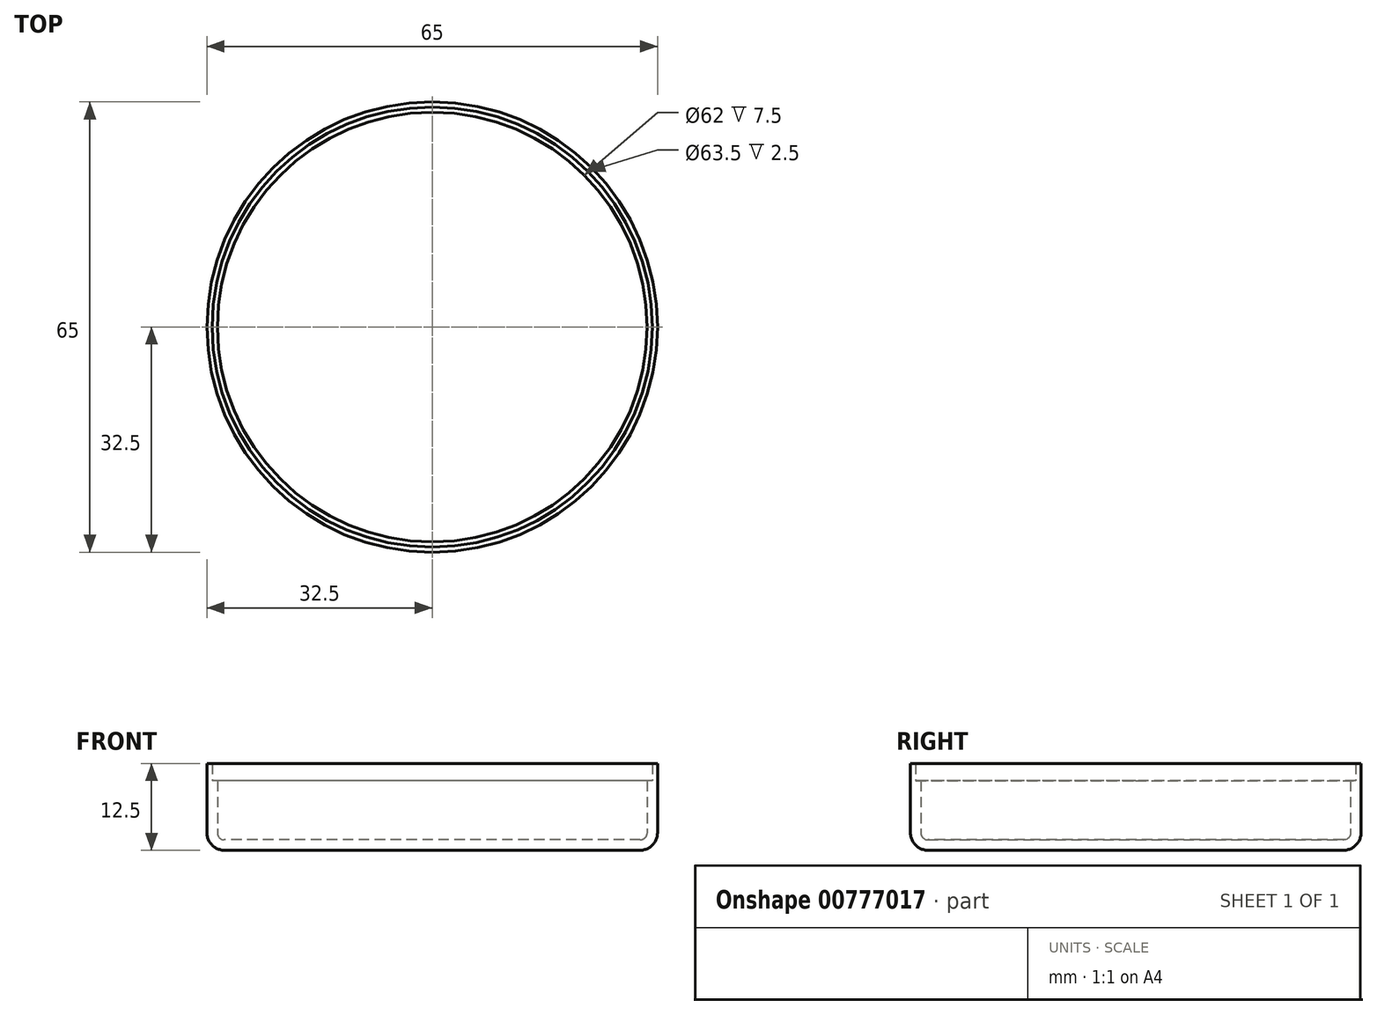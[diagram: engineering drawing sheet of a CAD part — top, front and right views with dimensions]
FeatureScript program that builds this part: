
annotation { "Feature Type Name" : "Feature", "Feature Type Description" : "" }
export const myFeature = defineFeature(function(context is Context, id is Id, definition is map)
    precondition{}
    {
        {
            var Q0;
            Q0=qCreatedBy(makeId("Top.planeOp"),FACE);
            var sketch = newSketch(context, id + "F0", { "sketchPlane" : qUnion([Q0])});
            skCircle(sketch, "E0", {"center": v(0, 0) * mm, "radius": 32.5 * mm});
            skSolve(sketch);
        }
        {
            var Q0;
            Q0=qSketchRegion(id+"F0",true);
            extrude(context, id + "F1", {"entities" : qUnion([Q0]), "depth" : 10 * mm, "offsetDistance" : 25 * mm});
        }
        {
            var Q0;
            Q0=makeQuery(id+"F1.opExtrude","CAP_FACE",FACE,{"disambiguationData":[OSD([sQuery(id+"F0.wireOp",EDGE,"pcHNsLAs-uuIG-92PN-J4nV-sG1yAEwh4vms.bottom"),sQuery(id+"F0.wireOp",EDGE,"pcHNsLAs-uuIG-92PN-J4nV-sG1yAEwh4vms.top"),sQuery(id+"F0.wireOp",EDGE,"pcHNsLAs-uuIG-92PN-J4nV-sG1yAEwh4vms.left"),sQuery(id+"F0.wireOp",EDGE,"pcHNsLAs-uuIG-92PN-J4nV-sG1yAEwh4vms.right"),sQuery(id+"F0.wireOp",EDGE,"3d6bdb04-9177-4708-87b0-630207d0257c.filletArc"),sQuery(id+"F0.wireOp",EDGE,"a6119fb4-ba20-4dce-af5d-a38932c804a4.filletArc"),sQuery(id+"F0.wireOp",EDGE,"7038d429-74eb-4160-9e18-919da026d677.filletArc"),sQuery(id+"F0.wireOp",EDGE,"e058b54d-4a7d-470c-b5c4-87012d02d3e7.filletArc")])],"isStart":true});
            var Q1;
            Q1=makeQuery(id+"F1.opExtrude","CAP_FACE",FACE,{"disambiguationData":[OSD([sQuery(id+"F0.wireOp",EDGE,"E0")])],"isStart":true});
            fillet(context, id + "F2", {"entities" : qUnion([Q0, Q1]), "radius" : 2.5 * mm, "tangentPropagation" : true, "allowEdgeOverflow" : false});
        }
        {
            var Q0;
            Q0=makeQuery(id+"F1.opExtrude","CAP_FACE",FACE,{"disambiguationData":[OSD([sQuery(id+"F0.wireOp",EDGE,"pcHNsLAs-uuIG-92PN-J4nV-sG1yAEwh4vms.bottom"),sQuery(id+"F0.wireOp",EDGE,"pcHNsLAs-uuIG-92PN-J4nV-sG1yAEwh4vms.top"),sQuery(id+"F0.wireOp",EDGE,"pcHNsLAs-uuIG-92PN-J4nV-sG1yAEwh4vms.left"),sQuery(id+"F0.wireOp",EDGE,"pcHNsLAs-uuIG-92PN-J4nV-sG1yAEwh4vms.right"),sQuery(id+"F0.wireOp",EDGE,"3d6bdb04-9177-4708-87b0-630207d0257c.filletArc"),sQuery(id+"F0.wireOp",EDGE,"a6119fb4-ba20-4dce-af5d-a38932c804a4.filletArc"),sQuery(id+"F0.wireOp",EDGE,"7038d429-74eb-4160-9e18-919da026d677.filletArc"),sQuery(id+"F0.wireOp",EDGE,"e058b54d-4a7d-470c-b5c4-87012d02d3e7.filletArc")])],"isStart":false});
            var Q1;
            Q1=makeQuery(id+"F1.opExtrude","CAP_FACE",FACE,{"disambiguationData":[OSD([sQuery(id+"F0.wireOp",EDGE,"E0")])],"isStart":false});
            shell(context, id + "F3", {"entities" : qUnion([Q0, Q1]), "thickness" : 1.5 * mm});
        }
        {
            var Q0;
            Q0=makeQuery(id+"F1.opExtrude","CAP_FACE",FACE,{"disambiguationData":[OSD([sQuery(id+"F0.wireOp",EDGE,"E0")])],"isStart":false});
            var sketch = newSketch(context, id + "F4", { "sketchPlane" : qUnion([Q0])});
            skCircle(sketch, "E1.0", {"center": v(0, 0) * mm, "radius": 32.5 * mm});
            skCircle(sketch, "E2.0", {"center": v(0, 0) * mm, "radius": 31.75 * mm});
            skSolve(sketch);
        }
        {
            var Q0;
            Q0=qSketchRegion(id+"F4",true);
            extrude(context, id + "F5", {"entities" : qUnion([Q0]), "operationType" : NewBodyOperationType.ADD, "depth" : 2.5 * mm, "offsetDistance" : 25 * mm});
        }
    });
